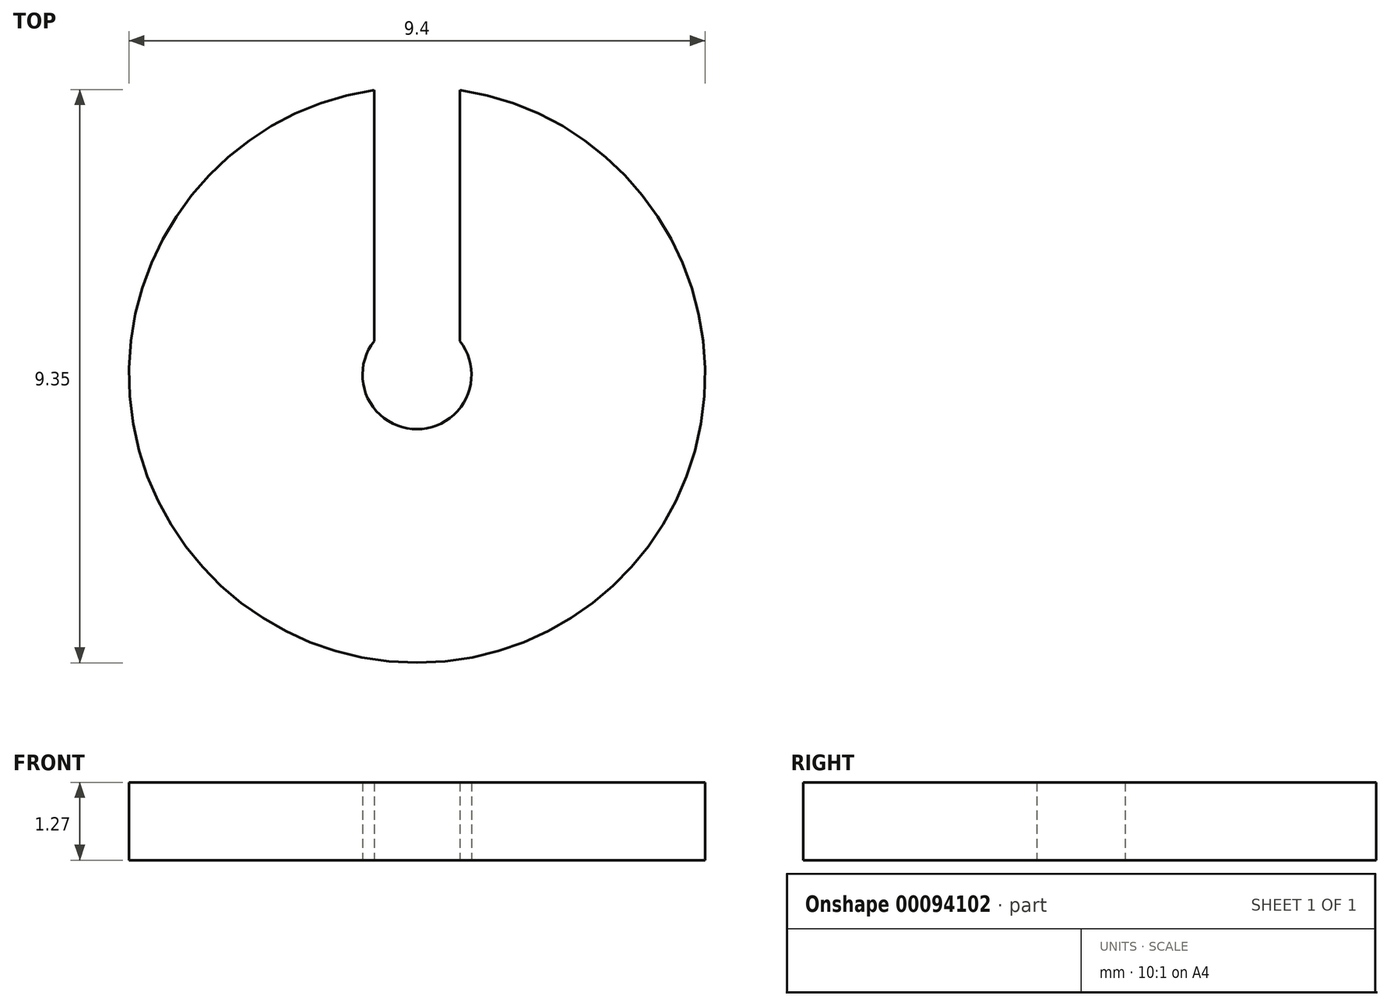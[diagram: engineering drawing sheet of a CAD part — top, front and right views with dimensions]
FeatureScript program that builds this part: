
annotation { "Feature Type Name" : "Feature", "Feature Type Description" : "" }
export const myFeature = defineFeature(function(context is Context, id is Id, definition is map)
    precondition{}
    {
        {
            var Q0;
            Q0=qCreatedBy(makeId("Top.planeOp"),FACE);
            var sketch = newSketch(context, id + "F0", { "sketchPlane" : qUnion([Q0])});
            skCircle(sketch, "E0", {"center": v(0, 0) * mm, "radius": 4.7 * mm});
            skCircle(sketch, "E1", {"center": v(0, 0) * mm, "radius": 0.89 * mm});
            skLineSegment(sketch, "E2.bottom", {"start": v(-0.7, 4.65) * mm, "end": v(0.7, 4.65) * mm});
            skLineSegment(sketch, "E2.top", {"start": v(-0.7, 0.55) * mm, "end": v(0.7, 0.55) * mm});
            skLineSegment(sketch, "E2.left", {"start": v(-0.7, 4.65) * mm, "end": v(-0.7, 0.55) * mm});
            skLineSegment(sketch, "E2.right", {"start": v(0.7, 4.65) * mm, "end": v(0.7, 0.55) * mm});
            skSolve(sketch);
        }
        {
            var Q0;
            {var subQ0=sQuery(id+"F0.wireOp",EDGE,"E2.left");Q0=makeQuery(id+"F0.imprint","IMPRINT",FACE,{"disambiguationData":[TD([[makeQuery(id+"F0.imprint","IMPRINT",EDGE,{"derivedFrom":subQ0}),-1.0]])]});}
            extrude(context, id + "F1", {"entities" : qUnion([Q0]), "depth" : 1.27 * mm});
        }
    });
